# Revit family: Drain_Floor_13.5_Inch_Square_Top-Zurn-Z675_Heavy-duty
name_source: partatom
category: Plumbing Fixtures
units: mm (PartAtom-declared; Revit-internal decimal feet)

## family parameters
Always vertical = Yes
Cut with Voids When Loaded = No
Maintain Annotation Orientation = No
OmniClass Number = 23.45.55.21
OmniClass Title = Drains (Wastes)
Part Type = Normal
Room Calculation Point = No
Round Connector Dimension = Use Radius
Shared = No
Work Plane-Based = No

## types (9) — shared parameters
Approx. Weight (Lbs) = 110 "
Assembly Code = D2030300
CW Connection = No
Default Elevation = 20 "
Description = 13.5 INCH SQUARE EXTRA HEAVY-DUTY DRAIN
Grate Open Area (Sq. In.) = 72 in²
HW Connection = No
Main Material = Iron - Zurn - Cast - Painted - Blue
Manufacturer = Zurn Water, LLC
Manufacurer Brand = Zurn
Model = Z675
Modified Date = 26/12/2025
Product Documentation Link = https://files.zurn.com
Product Installation Sheet URL = https://files.zurn.com
Product Page URL = https://www.zurn.com
Product data url = https://www.bimobject.com
URL = www.zurn.com
Vent Connection = No
WFU = 1
Waste Connection = Yes
zero-valued in all types: CWFU, HWFU

## per-type parameters (varying)
| type | Body Height_E | Connector Radius | Pipe Size_A Inside Diameter | Pipe Size_A Nominal Diameter | Pipe Size_A Outer Diameter | Type Comments |
| Z675-3IP | 7.125 " | 1.5 " | 3.068 " | 3 " | 3.5 " | Z675 - 3 Inch Threaded Outlet |
| Z675-3NH | 9.625 " | 1.5 " | 3.068 " | 3 " | 3.5 " | Z675 - 3 Inch No-Hub Outlet |
| Z675-3NL | 7.625 " | 1.5 " | 3.068 " | 3 " | 3.5 " | Z675 - 3 Inch Neo-Loc Outlet |
| Z675-4IC | 9.625 " | 2 " | 4.028 " | 4 " | 4.5 " | Z675 - 4 Inch Inside Caulk Outlet |
| Z675-4IP | 7.125 " | 2 " | 4.028 " | 4 " | 4.5 " | Z675 - 4 Inch Threaded Outlet |
| Z675-4NH | 9.625 " | 2 " | 4.028 " | 4 " | 4.5 " | Z675 - 4 Inch No-Hub Outlet |
| Z675-4NL | 7.625 " | 2 " | 4.028 " | 4 " | 4.5 " | Z675 - 4 Inch Neo-Loc Outlet |
| Z675-6IP | 7.125 " | 3 " | 6.065 " | 6 " | 6.625 " | Z675 - 6 Inch Threaded Outlet |
| Z675-6NH | 9.625 " | 3 " | 6.065 " | 6 " | 6.625 " | Z675 - 6 Inch No-Hub Outlet |

## geometry (parser evidence)
native form markers: Sweep x2
no freeform markers — native parametric forms only
